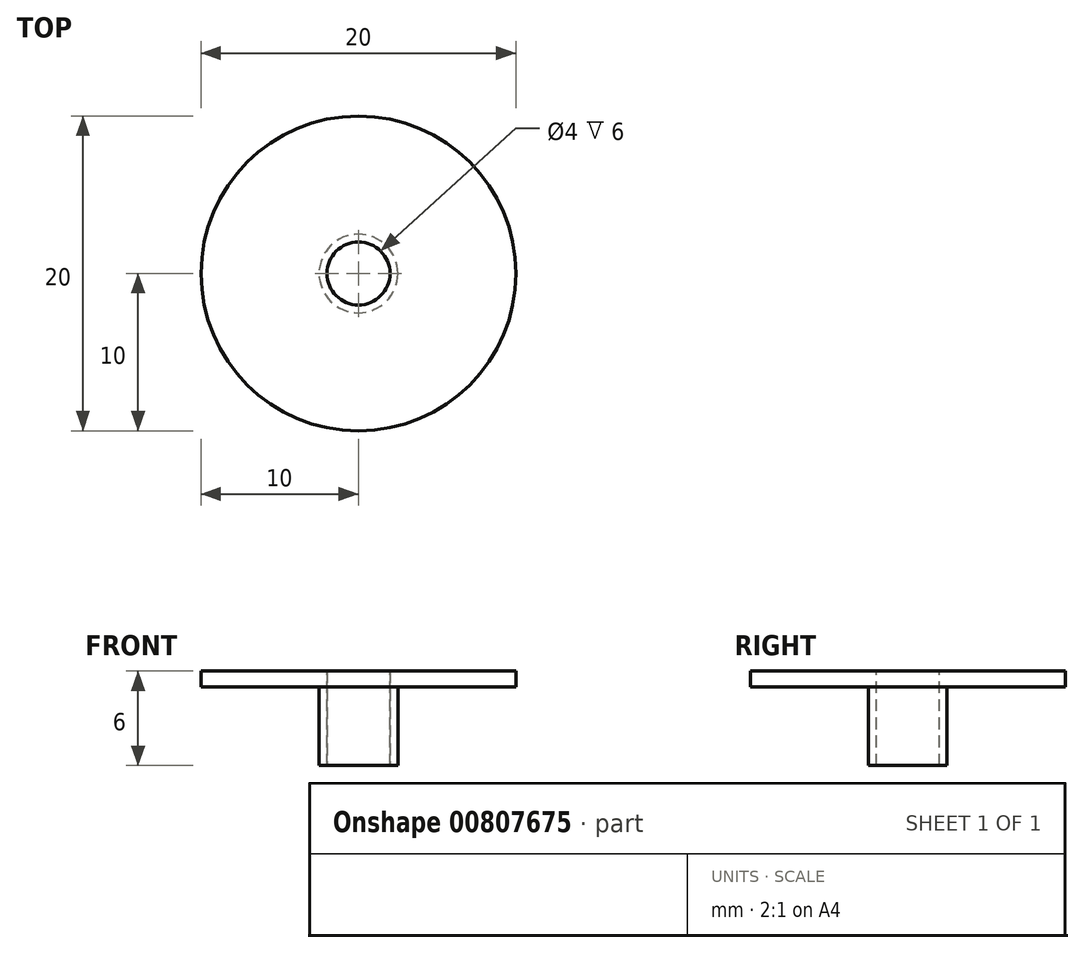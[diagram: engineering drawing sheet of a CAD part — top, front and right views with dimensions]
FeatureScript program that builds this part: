
annotation { "Feature Type Name" : "Feature", "Feature Type Description" : "" }
export const myFeature = defineFeature(function(context is Context, id is Id, definition is map)
    precondition{}
    {
        {
            var Q0;
            Q0=qCreatedBy(makeId("Top.planeOp"),FACE);
            var sketch = newSketch(context, id + "F0", { "sketchPlane" : qUnion([Q0])});
            skCircle(sketch, "E0", {"center": v(0, 0) * mm, "radius": 2.5 * mm});
            skSolve(sketch);
        }
        {
            var Q0;
            Q0 = qSketchRegion(id + "F0", true);
            extrude(context, id + "F1", {"entities" : qUnion([Q0]), "depth" : 5 * mm, "offsetDistance" : 25 * mm});
        }
        {
            var Q0;
            Q0=makeQuery(id+"F1.opExtrude","CAP_FACE",FACE,{"disambiguationData":[OSD([sQuery(id+"F0.wireOp",EDGE,"E0")])],"isStart":false});
            var sketch = newSketch(context, id + "F2", { "sketchPlane" : qUnion([Q0])});
            skCircle(sketch, "E1", {"center": v(0, 0) * mm, "radius": 10 * mm});
            skSolve(sketch);
        }
        {
            var Q0;
            Q0 = qSketchRegion(id + "F2", true);
            extrude(context, id + "F3", {"entities" : qUnion([Q0]), "operationType" : NewBodyOperationType.ADD, "depth" : 1 * mm, "offsetDistance" : 25 * mm});
        }
        {
            var Q0;
            Q0=makeQuery(id+"F1.opExtrude","CAP_FACE",FACE,{"disambiguationData":[OSD([sQuery(id+"F0.wireOp",EDGE,"E0")])],"isStart":true});
            var sketch = newSketch(context, id + "F4", { "sketchPlane" : qUnion([Q0])});
            skCircle(sketch, "E2", {"center": v(0, 0) * mm, "radius": 2 * mm});
            skSolve(sketch);
        }
        {
            var Q0;
            Q0 = qSketchRegion(id + "F4", true);
            extrude(context, id + "F5", {"entities" : qUnion([Q0]), "operationType" : NewBodyOperationType.REMOVE, "oppositeDirection" : true, "depth" : 25 * mm, "offsetDistance" : 25 * mm});
        }
        {
            var Q0;
            Q0=makeQuery(id+"F3.opExtrude","CAP_FACE",FACE,{"disambiguationData":[OSD([sQuery(id+"F2.wireOp",EDGE,"E1")])],"isStart":false});
            var sketch = newSketch(context, id + "F6", { "sketchPlane" : qUnion([Q0])});
            skCircle(sketch, "E3", {"center": v(0, 0) * mm, "radius": 2 * mm});
            skSolve(sketch);
        }
        {
            var Q0;
            Q0=makeQuery(id+"F6.imprint","IMPRINT",FACE,{"disambiguationData":[TD([[makeQuery(id+"F6.imprint","IMPRINT",EDGE,{"derivedFrom":sQuery(id+"F6.wireOp",EDGE,"E3")}),1.0]])]});
            extrude(context, id + "F7", {"entities" : qUnion([Q0]), "oppositeDirection" : true, "depth" : 6 * mm, "offsetDistance" : 25 * mm});
        }
    });
